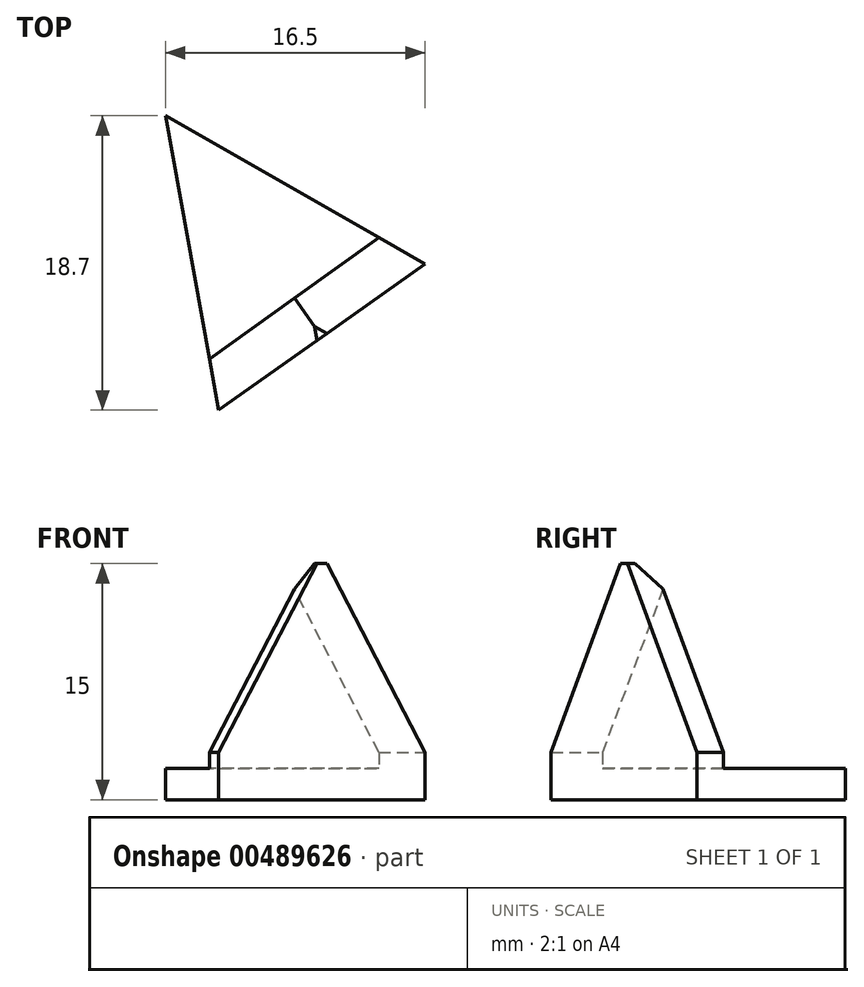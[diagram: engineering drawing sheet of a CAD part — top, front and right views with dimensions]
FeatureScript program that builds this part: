
annotation { "Feature Type Name" : "Feature", "Feature Type Description" : "" }
export const myFeature = defineFeature(function(context is Context, id is Id, definition is map)
    precondition{}
    {
        {
            var Q0;
            Q0=qCreatedBy(makeId("Top.planeOp"),FACE);
            var sketch = newSketch(context, id + "F0", { "sketchPlane" : qUnion([Q0])});
            skLineSegment(sketch, "E0.0", {"start": v(-7.34, 9.49) * mm, "end": v(9.16, 0.07) * mm});
            skLineSegment(sketch, "E0.1", {"start": v(9.16, 0.07) * mm, "end": v(-3.95, -9.2) * mm});
            skLineSegment(sketch, "E0.2", {"start": v(-3.95, -9.2) * mm, "end": v(-7.34, 9.49) * mm});
            skPoint(sketch, "E0.0.midPoint", {"position": v(0.9, 4.78) * mm});
            skLineSegment(sketch, "E1", {"start": v(-4.54, -5.96) * mm, "end": v(6.21, 1.75) * mm});
            skSolve(sketch);
        }
        {
            var Q0;
            Q0 = qSketchRegion(id + "F0", true);
            extrude(context, id + "F1", {"entities" : qUnion([Q0]), "depth" : 2 * mm, "offsetDistance" : 25 * mm});
        }
        {
            var Q0;
            {var subQ0=sQuery(id+"F0.wireOp",EDGE,"E0.1");Q0=makeQuery(id+"F0.imprint","IMPRINT",FACE,{"disambiguationData":[TD([[makeQuery(id+"F0.imprint","IMPRINT",EDGE,{"derivedFrom":subQ0}),-1.0]])]});}
            extrude(context, id + "F2", {"entities" : qUnion([Q0]), "operationType" : NewBodyOperationType.ADD, "depth" : 15 * mm, "offsetDistance" : 25 * mm});
        }
        {
            var Q0;
            Q0=makeQuery(id+"F2.opExtrude","CAP_EDGE",EDGE,{"disambiguationData":[OSD([sQuery(id+"F0.wireOp",EDGE,"E0.2")])],"isStart":false});
            var Q1;
            Q1=makeQuery(id+"F2.opExtrude","CAP_EDGE",EDGE,{"disambiguationData":[OSD([sQuery(id+"F0.wireOp",EDGE,"E0.0")])],"isStart":false});
            chamfer(context, id + "F3", {"entities" : qUnion([Q0, Q1]), "chamferType" : ChamferType.OFFSET_ANGLE, "width" : 12 * mm, "oppositeDirection" : false, "angle" : 30 * degree, "tangentPropagation" : true});
        }
    });
